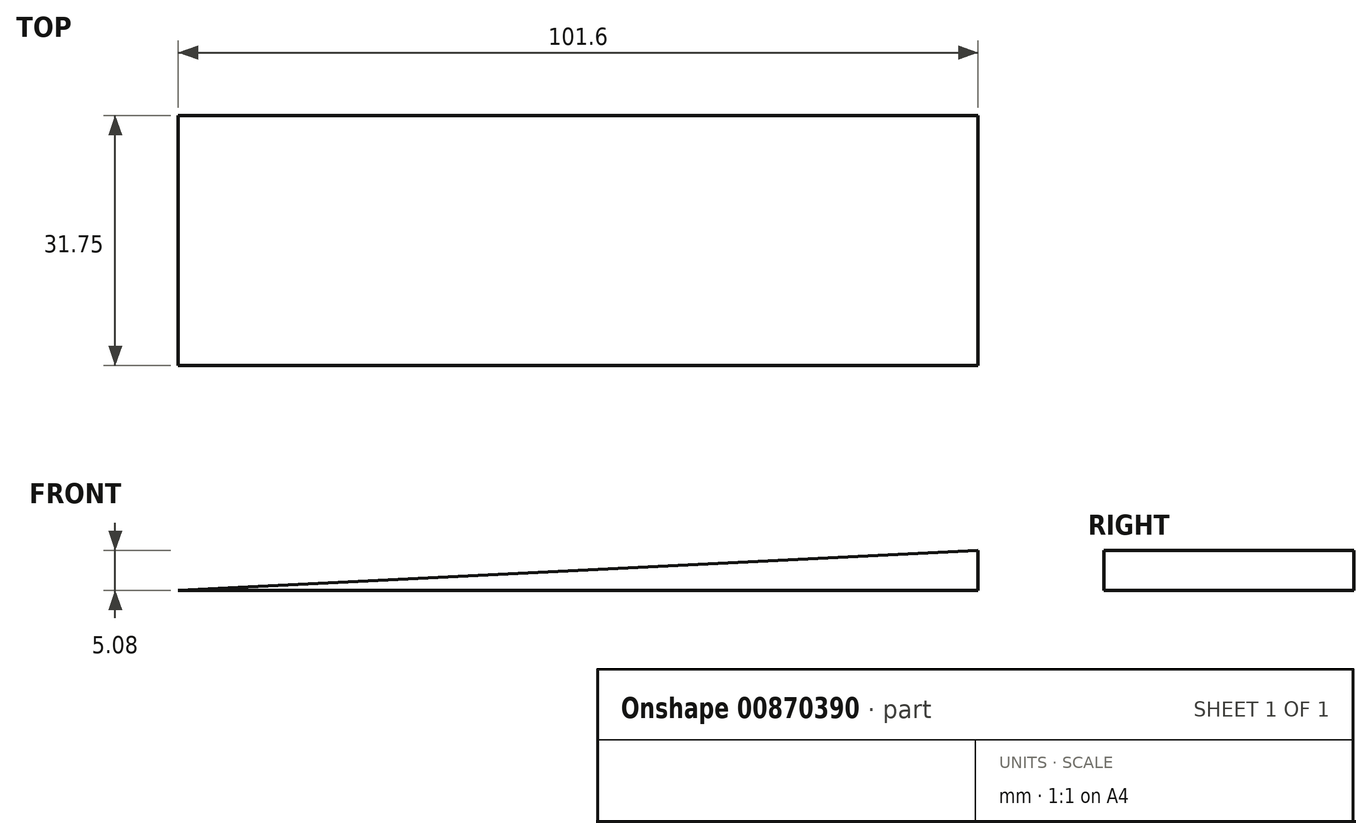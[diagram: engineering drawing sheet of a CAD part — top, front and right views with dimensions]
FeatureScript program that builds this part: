
annotation { "Feature Type Name" : "Feature", "Feature Type Description" : "" }
export const myFeature = defineFeature(function(context is Context, id is Id, definition is map)
    precondition{}
    {
        {
            var Q0;
            Q0=qCreatedBy(makeId("Front.planeOp"),FACE);
            var sketch = newSketch(context, id + "F0", { "sketchPlane" : qUnion([Q0])});
            skLineSegment(sketch, "E0", {"start": v(0, 0) * mm, "end": v(-101.6, 0) * mm});
            skLineSegment(sketch, "E1", {"start": v(0, 0) * mm, "end": v(0, 5.08) * mm});
            skLineSegment(sketch, "E2", {"start": v(-101.6, 0) * mm, "end": v(0, 5.08) * mm});
            skSolve(sketch);
        }
        {
            var Q0;
            Q0 = qSketchRegion(id + "F0", true);
            extrude(context, id + "F1", {"entities" : qUnion([Q0]), "depth" : 31.75 * mm, "offsetDistance" : 25.4 * mm});
        }
    });
